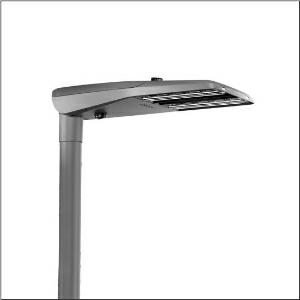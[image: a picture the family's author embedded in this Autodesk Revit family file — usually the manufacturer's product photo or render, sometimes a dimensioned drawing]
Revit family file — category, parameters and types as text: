
# Revit family: streetlight_sl_11_iq_midi___st1_0ab_5xc3n51y08me_91dd
name_source: partatom
category: Lighting Fixtures
units: mm (PartAtom-declared; Revit-internal decimal feet)

## family parameters
Cut with Voids When Loaded = No
Host = Face
Light Source = No
Part Type = Normal
Room Calculation Point = No
Round Connector Dimension = Use Diameter
Shared = No

## types (1)
- --- (1 x LED, 15260 lm, 122.7 W, 3000K)
    Apparent Load = 123 VA
    CIE Flux Codes = 29 63 95 100 100
    Color Rendering = 70
    Color Temperature = 3000K
    Default Elevation = 1800 mm
    Description = Streetlight SL 11 iQ midi, mast luminaire, primary light control with 3 zone facetted reflector, of plastic, silver coated, highly specular, primary optical cover: cover, of PMMA, transparent, light distribution: ST1.0aB, light emission: direct distribution, primary light characteristic: asymmetric, installation type: post-top, side-entry, lamps: LED, High Power LED, rated values: 15.260lm | 122,7W | 124,4lm/W (begin service life); end service life: 15.260lm | 130,2W; at 50% lumin. flux: 7.630lm | 56,1W | 136lm/W, colour temperature: 3000K, colour rendering: CRI > 70, light colour: 730, light setting 1 begin service life: 100% | 15.260lm | 122,7W | 124,4lm/W | 3.000K, light setting 1 end service life: 130,2W, further light settings possible, control: pre-setting: logarithmic dimming characteristic, Street-Remote, Auto-Match, Temp-Guard, Lumen-Switch, Night-Set, Smart-Wire, Light-Fading, Desk-Remote (wireless, voltage-free reading and setting of iQ features in the workshop via application-optimized NFC function/RFID function), optimised constant luminous flux control (CLO 2.0), with cable H07RN-F 5x 1.5mm², mains connection: 230..240V, AC, 50/60Hz, connection cable pre-assembled, cable length: 12,5m, luminaire housing, of diecast aluminium, powder-coated, Siteco® metallic grey (DB 702S), please order mast flange separately, inclination adjustable without tools: 0°, 5°, 10°, 15° (post-top) | 0°, -5°, -10°, -15° (side-entry), sealing non-destructively replaceable, multi-level sealing system, length: 780mm, width: 376mm, height: 118mm, mast flange for spigot size: 42mm (side-entry): 5XC10008XM4, 60/48mm (side-entry/post-top): 5XC10108XM2, 76/60mm (side-entry/post-top): 5XC10108XM1, equipment: Power, Smart Interface below and above, protection rating (complete): IP66, insulation class (complete): insulation class II (safety insulation), certification: CE, ENEC, ENEC+, VDE, UKCA, impact resistance: IK10, permissible operating ambient temperature for outdoor applications: -25..+50°C, standard-compliant lighting for roads and squares, Environmental Product Declaration (EPD) tested and certified by an independent institute, packaging unit: 1 piece

Light Distribution: ST1.0aB
    Height = 118 mm
    Lamp = 1 x LED
    Lamp Light Flux = 15260 lm
    Lamp Power = 122.7 W
    Lamp count = 1
    Length = 780 mm
    Luminous efficacy = 124 lm/W
    Manufacturer = Siteco
    ModVariant = No
    Model = 5XC3N51Y08ME
    Number of Poles = 1
    OnlyDefault = Yes
    Power Factor = 1
    Product Name = Streetlight SL 11 iQ midi | ST1.0aB
    Product group = mast luminaire | pylon top
    ProductGroupID = 6100
    Protection Class = Protection class II
    Protection Degree = IP 66
    RLX_Detail_Level = 1
    RLX_Emergency_Light_Flux = 0 lm
    RLX_Emergency_Type = 0
    RLX_Emergency_Type_DB = No
    RlxData = <blob elided: 69337 chars, md5=b8557aba>
    Socket = socket
    Standby Power = 0 W
    System Light Flux = 15260 lm
    System Power = 123 W
    Type Comments = factory setting: luminous flux: 100 % | dim-lin: 254 | 552 mA
    Type Image = l_1004429.jpg
    URL = http://relux.com
    VarID = @adj_109371
    Voltage = 0 V
    Weight = 0.00 kg
    Width = 376 mm

## geometry (parser evidence)
native form markers: Blend x4, Sweep x10
no freeform markers — native parametric forms only
